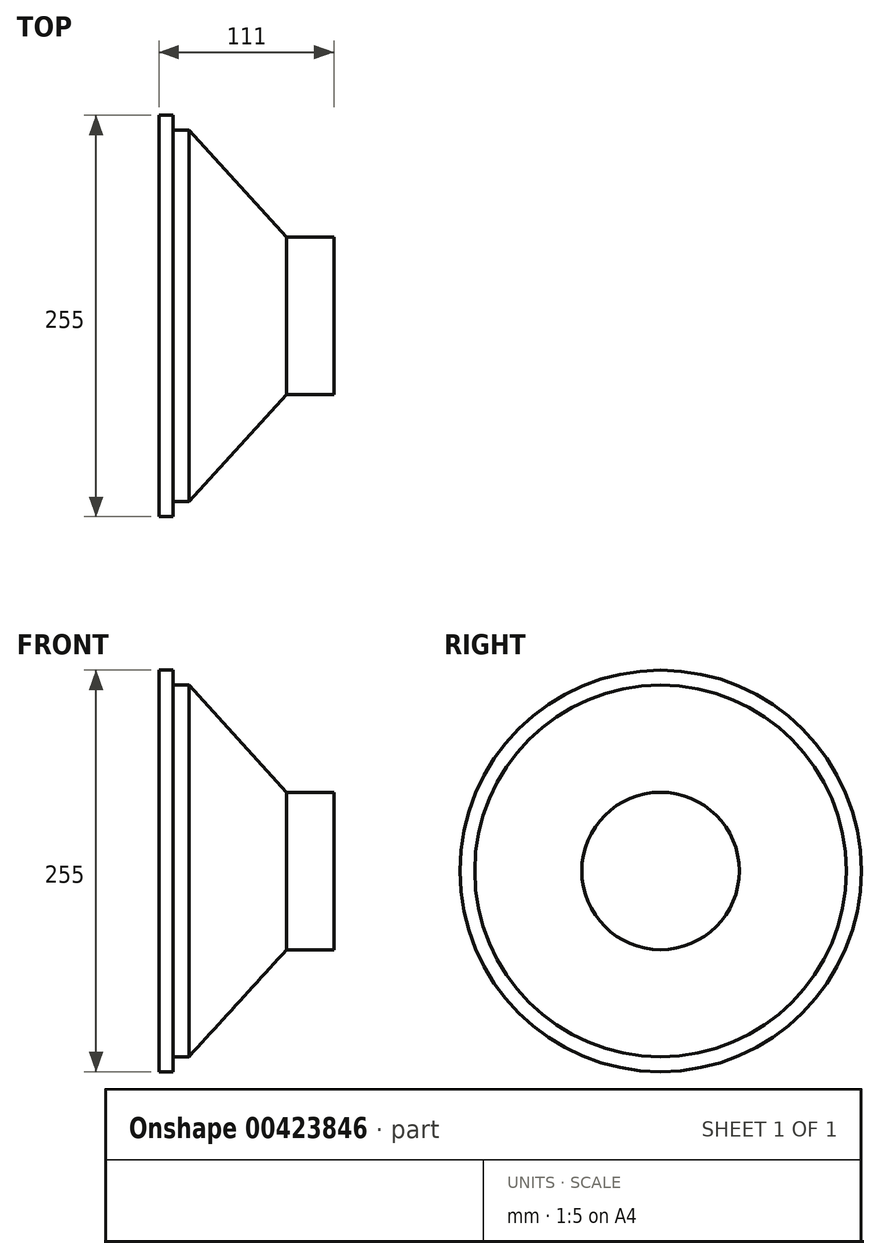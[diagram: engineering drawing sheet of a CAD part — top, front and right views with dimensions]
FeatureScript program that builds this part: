
annotation { "Feature Type Name" : "Feature", "Feature Type Description" : "" }
export const myFeature = defineFeature(function(context is Context, id is Id, definition is map)
    precondition{}
    {
        {
            var Q0;
            Q0=qCreatedBy(makeId("Front.planeOp"),FACE);
            var sketch = newSketch(context, id + "F0", { "sketchPlane" : qUnion([Q0])});
            skLineSegment(sketch, "E0", {"start": v(0, 0) * mm, "end": v(0, 127.5) * mm});
            skLineSegment(sketch, "E1", {"start": v(0, 127.5) * mm, "end": v(9, 127.5) * mm});
            skLineSegment(sketch, "E2", {"start": v(9, 127.5) * mm, "end": v(9, 118) * mm});
            skLineSegment(sketch, "E3", {"start": v(9, 118) * mm, "end": v(19, 118) * mm});
            skLineSegment(sketch, "E4", {"start": v(19, 118) * mm, "end": v(81, 50) * mm});
            skLineSegment(sketch, "E5", {"start": v(81, 50) * mm, "end": v(111, 50) * mm});
            skLineSegment(sketch, "E6", {"start": v(111, 50) * mm, "end": v(111, 0) * mm});
            skLineSegment(sketch, "E7", {"start": v(111, 0) * mm, "end": v(0, 0) * mm});
            skSolve(sketch);
        }
        {
            var Q0;
            Q0=qSketchRegion(id+"F0",true);
            var Q1;
            Q1=sQuery(id+"F0.wireOp",EDGE,"E7");
            revolve(context, id + "F1", {"entities" : qUnion([Q0]), "axis" : qUnion([Q1]), "revolveType" : RevolveType.FULL});
        }
    });
